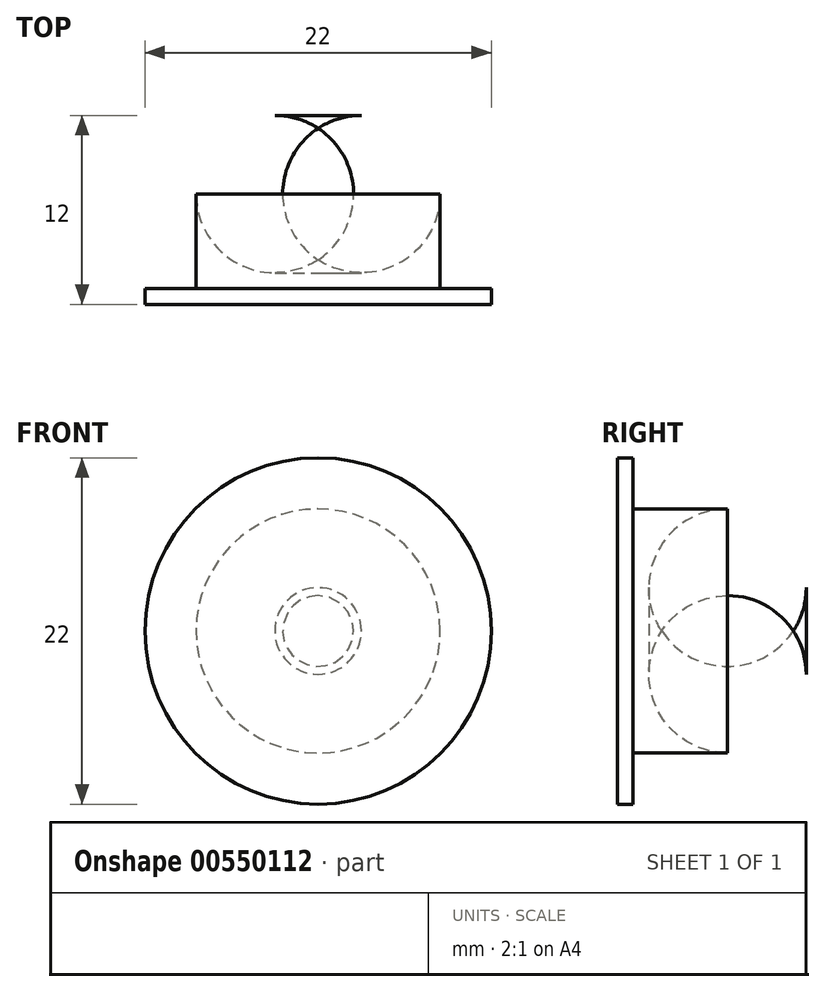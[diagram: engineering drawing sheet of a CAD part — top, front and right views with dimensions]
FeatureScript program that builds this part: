
annotation { "Feature Type Name" : "Feature", "Feature Type Description" : "" }
export const myFeature = defineFeature(function(context is Context, id is Id, definition is map)
    precondition{}
    {
        {
            var Q0;
            Q0=qCreatedBy(makeId("Front.planeOp"),FACE);
            var sketch = newSketch(context, id + "F0", { "sketchPlane" : qUnion([Q0])});
            skCircle(sketch, "E0", {"center": v(0, 0) * mm, "radius": 7.75 * mm});
            skCircle(sketch, "E1", {"center": v(0, 0) * mm, "radius": 11 * mm});
            skSolve(sketch);
        }
        {
            var Q0;
            Q0=makeQuery(id+"F0.imprint","IMPRINT",FACE,{"disambiguationData":[TD([[makeQuery(id+"F0.imprint","IMPRINT",EDGE,{"derivedFrom":sQuery(id+"F0.wireOp",EDGE,"E0")}),1.0]])]});
            extrude(context, id + "F1", {"entities" : qUnion([Q0]), "oppositeDirection" : true, "depth" : 12 * mm, "offsetDistance" : 25 * mm});
        }
        {
            var Q0;
            Q0 = qSketchRegion(id + "F0", true);
            extrude(context, id + "F2", {"entities" : qUnion([Q0]), "operationType" : NewBodyOperationType.ADD, "oppositeDirection" : true, "depth" : 1 * mm, "offsetDistance" : 25 * mm});
        }
        {
            var Q0;
            Q0=makeQuery(id+"F1.opExtrude","CAP_EDGE",EDGE,{"disambiguationData":[OSD([sQuery(id+"F0.wireOp",EDGE,"E0")])],"isStart":false});
            fillet(context, id + "F3", {"entities" : qUnion([Q0]), "radius" : 5 * mm, "tangentPropagation" : true, "allowEdgeOverflow" : false});
        }
    });
